# Revit family: Condensing-Storage-Water-Heater-Gas-AO_Smith-TWI-45-190_G
name_source: partatom
category: Mechanical Equipment
revit_build: Autodesk Revit 2014 (Build: 20130308_1515(x64)
units: mm (PartAtom-declared; Revit-internal decimal feet)

## types (1)
- Condensing-Storage-Water-Heater-Gas-AO_Smith-TWI-45-190_G
    (Additional Control) Frequency = 0 Hz
    (Additional Control) Phase = 1
    (Additional Control) Power Consumption (nominal) = 0 W
    (Additional Control) Voltage = 0 V
    1e Maintenance (check-up) = 3 months after installation
    2nd Maintenance (general maintenance) = 12 months after installation
    APS Pressure < = 400.0 Pa
    Assembly Code = D3010
    BIM Content Developer = CAD & Company
    CE-PIN = 0063BO5142
    Co2 Emissions (tol. +/- 1.0) vol% = 9.3
    Cold Water Connection R = 1"
    Condens Discharge Connection = 1 mm  [stored 0.00328084 ft]
    Default Setpoint = 65 °C
    Description = Condensing High Efficiency Storage Water Heater
    Destination / Country = UK & Ireland
    Diameter = 730 mm
    Drain Valve Connection Rp = 3/4"
    Draw-off Capacity @ ΔT = 28°C after 120 min. = 3300.0 L
    Draw-off Capacity @ ΔT = 28°C after 30 min. = 1100.0 L
    Draw-off Capacity @ ΔT = 28°C after 60 min. = 1900.0 L
    Draw-off Capacity @ ΔT = 28°C after 90 min. = 2600.0 L
    Draw-off Capacity @ ΔT = 44°C after 120 min. = 2100.0 L
    Draw-off Capacity @ ΔT = 44°C after 30 min. = 670.0 L
    Draw-off Capacity @ ΔT = 44°C after 60 min. = 1200.0 L
    Draw-off Capacity @ ΔT = 44°C after 90 min. = 1600.0 L
    Draw-off Capacity @ ΔT = 50°C after 120 min. = 1900.0 L
    Draw-off Capacity @ ΔT = 50°C after 30 min. = 580.0 L
    Draw-off Capacity @ ΔT = 50°C after 60 min. = 990.0 L
    Draw-off Capacity @ ΔT = 50°C after 90 min. = 1400.0 L
    Draw-off Capacity @ ΔT = 55°C after 120 min. = 1700.0 L
    Draw-off Capacity @ ΔT = 55°C after 30 min. = 520.0 L
    Draw-off Capacity @ ΔT = 55°C after 60 min. = 890.0 L
    Draw-off Capacity @ ΔT = 55°C after 90 min. = 1300.0 L
    Draw-off Capacity @ ΔT = 70°C after 120 min. = 1300.0 L
    Draw-off Capacity @ ΔT = 70°C after 30 min. = 380.0 L
    Draw-off Capacity @ ΔT = 70°C after 60 min. = 670.0 L
    Draw-off Capacity @ ΔT = 70°C after 90 min. = 970.0 L
    Empty Weight = 82 kg
    Energy Efficiency Rating (Hi, acc NEN-EN 89-1999) = 106
    Energy Efficiency Rating (Hs, acc NEN-EN 89-1999) = 95
    Flue Diameter - concentric system = 100/150 mm/mm
    Flue Diameter - parallel system = 100 mm  [stored 0.328084 ft]
    Flue Diameter - water heater = 100/150 mm/mm
    Frequency = 50 Hz
    Gas Category = I2H
    Gas Connection R = 1/2"
    Gas Flow Rate - Mass kg/h = 0
    Gas Flow Rate - Volume ltr/hr = 4.8
    Heating Up Time @ ΔT = 28°C = 8
    Heating Up Time @ ΔT = 44°C = 12
    Heating Up Time @ ΔT = 50°C = 14
    Heating Up Time @ ΔT = 55°C = 15
    Heating Up Time @ ΔT = 70°C = 19
    Height = 1655 mm
    Height Air Inlet = 385 mm
    Height Cold water Intlet = 400 mm  [stored 1.31234 ft]
    Height Flue Outlet = 385 mm
    Height Gas Connection = 160 mm  [stored 0.524934 ft]
    Height Warm Water Outlet = 1655 mm
    Hot / Warm Water Connection R = 1"
    Installation Type = B23/C13/C33/C43/C53/C63
    Insulation Thickness = 50 mm  [stored 0.164042 ft]
    Length = 0 mm  [stored 0 ft]
    Maintenance Interval = 12
    Manufacturer = A.O. Smith Water Products Company b.v.
    Manufacturer Number = E 7110
    Max. Flue Gas Outlet Temperature = 65 °C
    Max. Operating Pressure = 800000.0 Pa
    Max. Setpoint = 85 °C
    Min. Setpoint = 10 °C
    Model = TWI 45 -190 G
    NOx Emissions (air free, 0% O2) ppm = 16
    NOx Emissions mg/kWh = 29
    Noice-level dB (A) = 58
    Nominal Heat Input (Gross) = 50000 W
    Nominal Heat Input (Net) = 45000 W
    Nominal Output = 47700 W
    Operating Weight = 271 kg
    Packaging Height = 1750 mm
    Packaging Length = 870 mm
    Packaging Width = 780 mm
    Phase = 1
    Power Consumption (nominal) = 300 W
    Product Documentation Link = http://www.aosmithinternational.com
    Product Instruction Link = http://www.aosmithinternational.com
    Recovery Rate @ ΔT = 28°C = 1500.0 L/s
    Recovery Rate @ ΔT = 44°C = 940.0 L/s
    Recovery Rate @ ΔT = 50°C = 830.0 L/s
    Recovery Rate @ ΔT = 55°C = 750.0 L/s
    Recovery Rate @ ΔT = 70°C = 590.0 L/s
    Seasonal Energy Efficiency Rating = 91
    Serial Number = 8717449182281
    Stand-by Loss = 0 W
    Stand-by Loss - daily (24h) = 0 W
    Standard Set For = G20
    Storage Capacity = 189.0 L
    Supply Pressure = 2000.0 Pa
    T&P Connection Rp = 1"
    Transport Weight = 100 kg
    Type of Packaging = Plastic Shrink Wrap, Cardboard and Wood
    URL = www.aosmith.co.uk
    Voltage = 230 V
    Warranty on parts = 12 months
    Warranty on tank = 36 months
    Width = 0 mm  [stored 0 ft]

note: [stored X ft] marks values corroborated as IEEE doubles in the binary element streams (Revit-internal decimal feet)

## geometry (parser evidence)
native form markers: Blend x21, Sweep x21
no freeform markers — native parametric forms only
